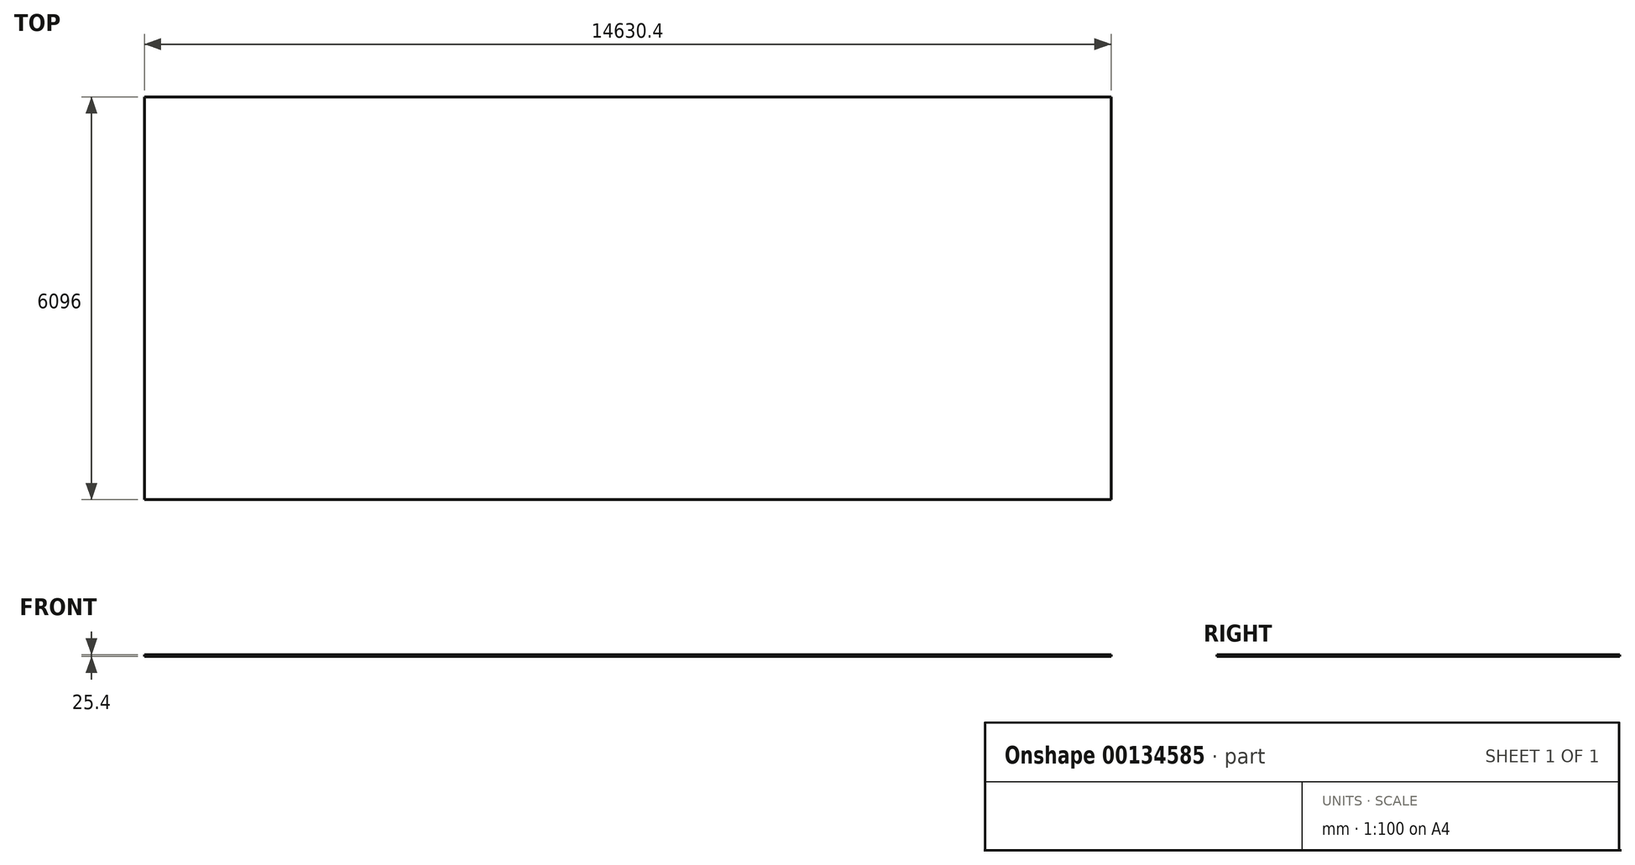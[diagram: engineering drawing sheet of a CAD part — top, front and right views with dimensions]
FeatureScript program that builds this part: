
annotation { "Feature Type Name" : "Feature", "Feature Type Description" : "" }
export const myFeature = defineFeature(function(context is Context, id is Id, definition is map)
    precondition{}
    {
        {
            var Q0;
            Q0=qCreatedBy(makeId("Top.planeOp"),FACE);
            var sketch = newSketch(context, id + "F0", { "sketchPlane" : qUnion([Q0])});
            skLineSegment(sketch, "E0.bottom", {"start": v(0, 0) * mm, "end": v(14630.4, 0) * mm});
            skLineSegment(sketch, "E0.top", {"start": v(0, -6096) * mm, "end": v(14630.4, -6096) * mm});
            skLineSegment(sketch, "E0.left", {"start": v(0, 0) * mm, "end": v(0, -6096) * mm});
            skLineSegment(sketch, "E0.right", {"start": v(14630.4, 0) * mm, "end": v(14630.4, -6096) * mm});
            skSolve(sketch);
        }
        {
            var Q0;
            Q0=makeQuery(id+"F0.imprint","IMPRINT",FACE,{"disambiguationData":[TD([[makeQuery(id+"F0.imprint","IMPRINT",EDGE,{"derivedFrom":sQuery(id+"F0.wireOp",EDGE,"E0.bottom")}),-1.0]])]});
            extrude(context, id + "F1", {"entities" : qUnion([Q0]), "oppositeDirection" : true, "depth" : 25.4 * mm});
        }
    });
